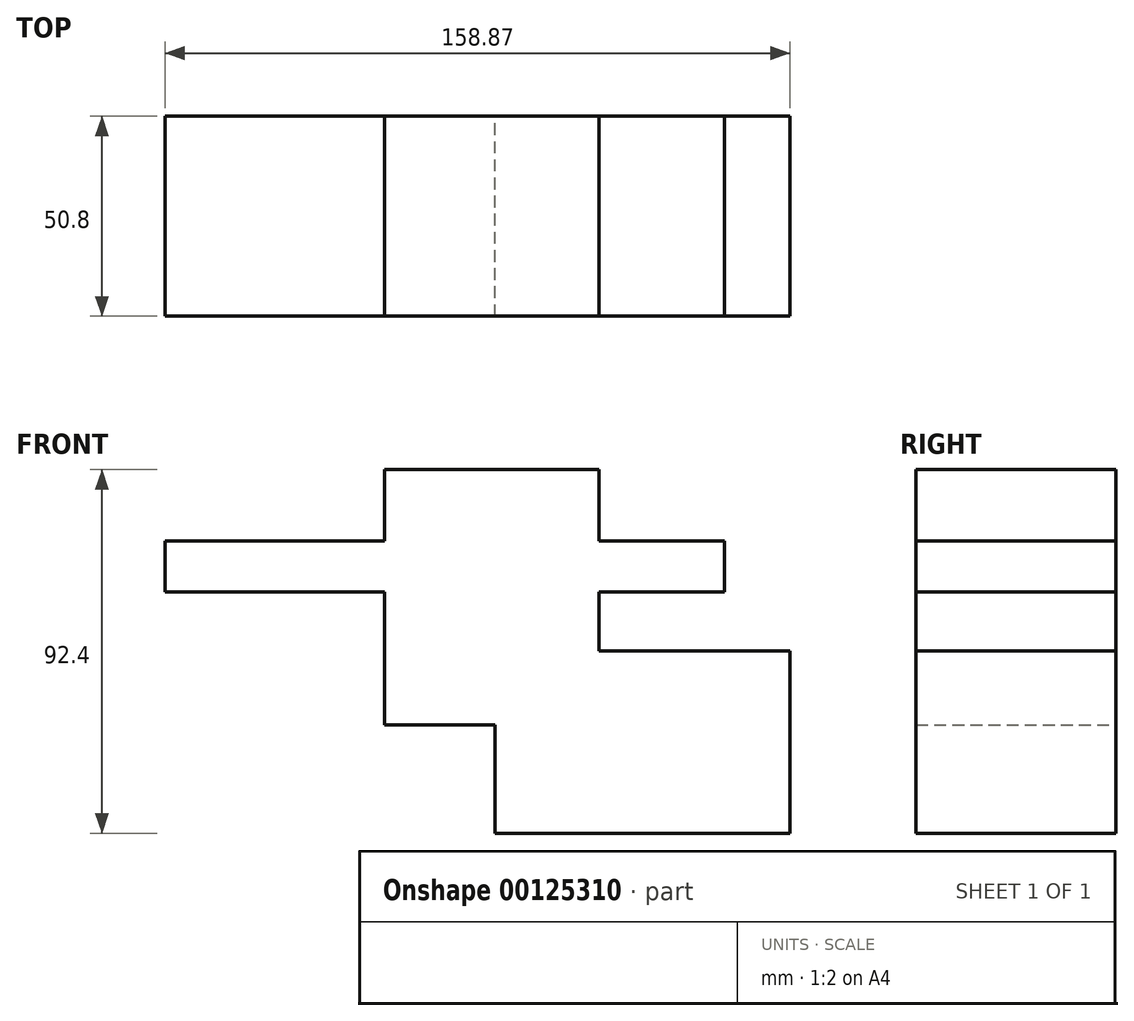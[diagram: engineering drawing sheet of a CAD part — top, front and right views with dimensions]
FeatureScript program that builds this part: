
annotation { "Feature Type Name" : "Feature", "Feature Type Description" : "" }
export const myFeature = defineFeature(function(context is Context, id is Id, definition is map)
    precondition{}
    {
        {
            var Q0;
            Q0=qCreatedBy(makeId("Front.planeOp"),FACE);
            var sketch = newSketch(context, id + "F0", { "sketchPlane" : qUnion([Q0])});
            skLineSegment(sketch, "E0.bottom", {"start": v(58.96, -49.64) * mm, "end": v(-16.08, -49.64) * mm});
            skLineSegment(sketch, "E0.top", {"start": v(58.96, -3.32) * mm, "end": v(-16.08, -3.32) * mm});
            skLineSegment(sketch, "E0.left", {"start": v(58.96, -49.64) * mm, "end": v(58.96, -3.32) * mm});
            skLineSegment(sketch, "E0.right", {"start": v(-16.08, -49.64) * mm, "end": v(-16.08, -3.32) * mm});
            skLineSegment(sketch, "E1.bottom", {"start": v(-44.1, -22.08) * mm, "end": v(10.32, -22.08) * mm});
            skLineSegment(sketch, "E1.top", {"start": v(-44.1, 42.76) * mm, "end": v(10.32, 42.76) * mm});
            skLineSegment(sketch, "E1.left", {"start": v(-44.1, -22.08) * mm, "end": v(-44.1, 42.76) * mm});
            skLineSegment(sketch, "E1.right", {"start": v(10.32, -22.08) * mm, "end": v(10.32, 42.76) * mm});
            skLineSegment(sketch, "E2.bottom", {"start": v(42.28, 11.73) * mm, "end": v(-99.91, 11.73) * mm});
            skLineSegment(sketch, "E2.top", {"start": v(42.28, 24.7) * mm, "end": v(-99.91, 24.7) * mm});
            skLineSegment(sketch, "E2.left", {"start": v(42.28, 11.73) * mm, "end": v(42.28, 24.7) * mm});
            skLineSegment(sketch, "E2.right", {"start": v(-99.91, 11.73) * mm, "end": v(-99.91, 24.7) * mm});
            skSolve(sketch);
        }
        {
            var Q0;
            Q0 = qSketchRegion(id + "F0", true);
            extrude(context, id + "F1", {"entities" : qUnion([Q0]), "endBound" : BoundingType.SYMMETRIC, "depth" : 50.8 * mm});
        }
    });
